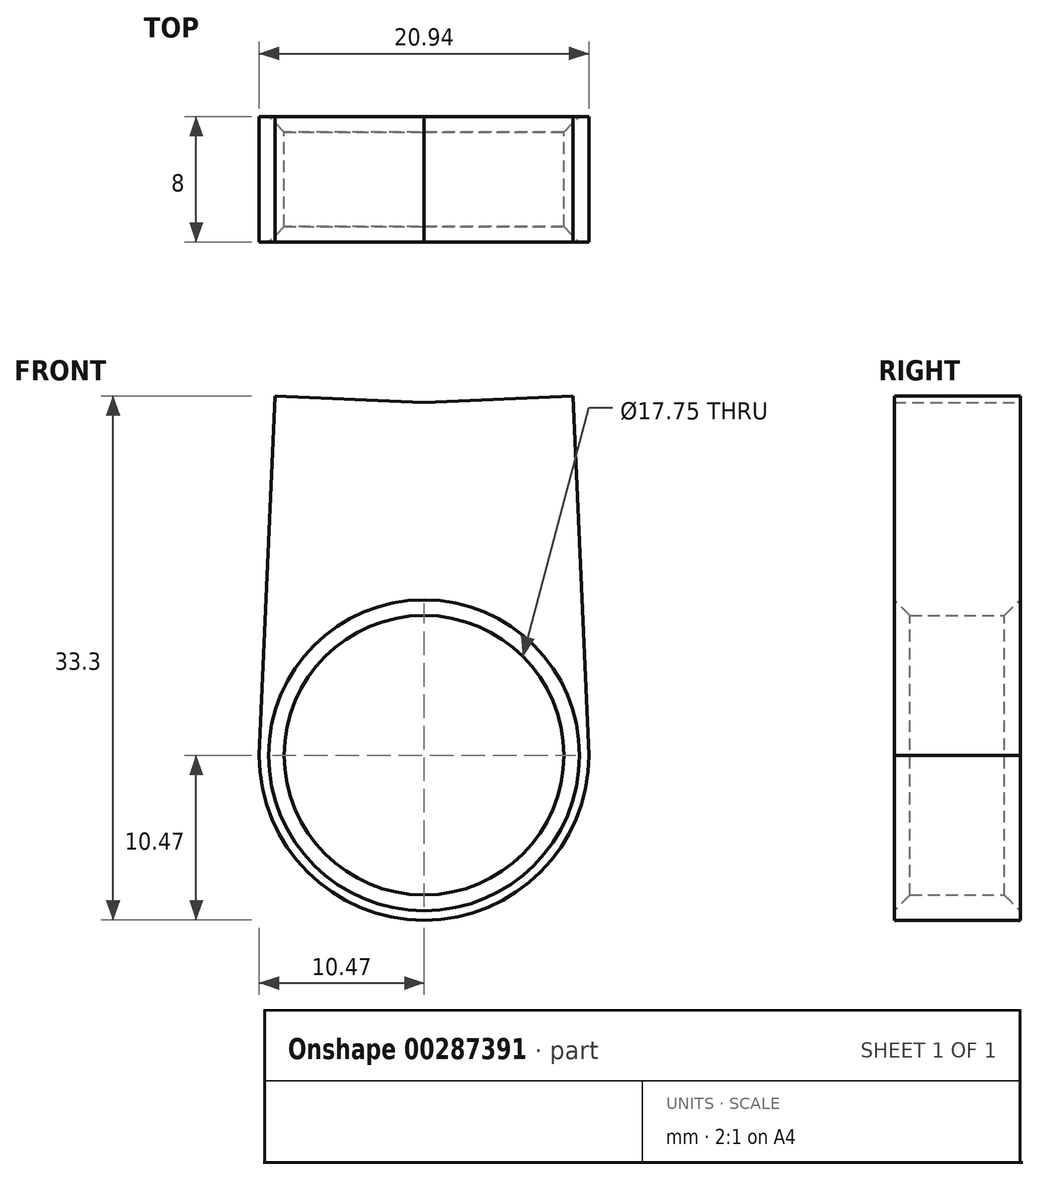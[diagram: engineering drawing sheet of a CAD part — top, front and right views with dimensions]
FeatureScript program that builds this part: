
annotation { "Feature Type Name" : "Feature", "Feature Type Description" : "" }
export const myFeature = defineFeature(function(context is Context, id is Id, definition is map)
    precondition{}
    {
        {
            var Q0;
            Q0=qCreatedBy(makeId("Front.planeOp"),FACE);
            var sketch = newSketch(context, id + "F0", { "sketchPlane" : qUnion([Q0])});
            skCircle(sketch, "E0", {"center": v(0, 0) * mm, "radius": 8.88 * mm});
            skCircle(sketch, "E1.0", {"center": v(0, 0) * mm, "radius": 10.48 * mm});
            skLineSegment(sketch, "E2", {"start": v(0, 10.47) * mm, "end": v(0.53, 22.39) * mm});
            skLineSegment(sketch, "E3", {"start": v(0.53, 22.39) * mm, "end": v(-9.46, 22.83) * mm});
            skLineSegment(sketch, "E4", {"start": v(-9.46, 22.83) * mm, "end": v(-10.48, 0) * mm});
            skLineSegment(sketch, "E5.MirrorCS", {"start": v(9.46, 22.83) * mm, "end": v(10.47, 0) * mm});
            skLineSegment(sketch, "E6.MirrorCS", {"start": v(-0.53, 22.39) * mm, "end": v(9.46, 22.83) * mm});
            skLineSegment(sketch, "E7.MirrorCS", {"start": v(0, 10.47) * mm, "end": v(-0.53, 22.39) * mm});
            skSolve(sketch);
        }
        {
            var Q0;
            {var subQ2=sQuery(id+"F0.wireOp",EDGE,"E5.MirrorCS");Q0=makeQuery(id+"F0.imprint","IMPRINT",FACE,{"disambiguationData":[TD([[makeQuery(id+"F0.imprint","IMPRINT",EDGE,{"derivedFrom":subQ2}),-1.0]])]});}
            var Q1;
            {var subQ0=sQuery(id+"F0.wireOp",EDGE,"E2");Q1=makeQuery(id+"F0.imprint","IMPRINT",FACE,{"disambiguationData":[TD([[makeQuery(id+"F0.imprint","IMPRINT",EDGE,{"derivedFrom":subQ0}),1.0]])]});}
            var Q2;
            Q2=makeQuery(id+"F0.imprint","IMPRINT",FACE,{"disambiguationData":[TD([[makeQuery(id+"F0.imprint","IMPRINT",EDGE,{"derivedFrom":sQuery(id+"F0.wireOp",EDGE,"E0")}),-1.0]])]});
            var Q3;
            {var subQ5=sQuery(id+"F0.wireOp",EDGE,"E7.MirrorCS");Q3=makeQuery(id+"F0.imprint","IMPRINT",FACE,{"disambiguationData":[TD([[makeQuery(id+"F0.imprint","IMPRINT",EDGE,{"derivedFrom":subQ5}),1.0]])]});}
            extrude(context, id + "F1", {"entities" : qUnion([Q0, Q1, Q2, Q3]), "depth" : 8 * mm});
        }
        {
            var Q0;
            Q0=makeQuery(id+"F1.opExtrude","CAP_EDGE",EDGE,{"disambiguationData":[OSD([sQuery(id+"F0.wireOp",EDGE,"E0")])],"isStart":true});
            var Q1;
            Q1=makeQuery(id+"F1.opExtrude","CAP_EDGE",EDGE,{"disambiguationData":[OSD([sQuery(id+"F0.wireOp",EDGE,"E0")])],"isStart":false});
            chamfer(context, id + "F2", {"entities" : qUnion([Q0, Q1]), "width" : 1 * mm, "tangentPropagation" : true});
        }
    });
